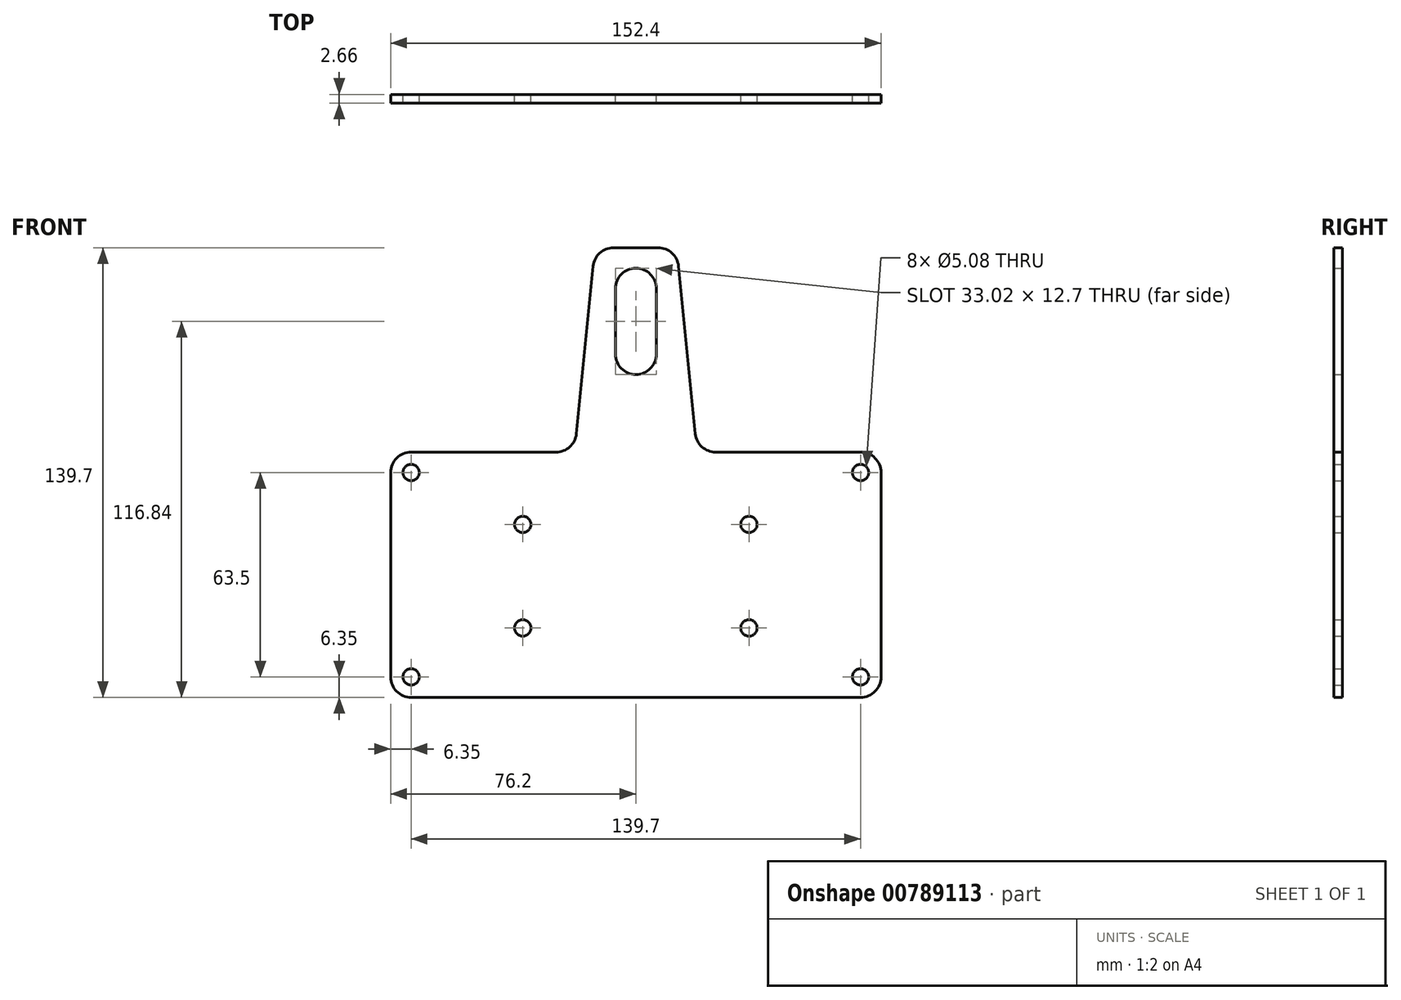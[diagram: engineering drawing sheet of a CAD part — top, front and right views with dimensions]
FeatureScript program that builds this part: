
annotation { "Feature Type Name" : "Feature", "Feature Type Description" : "" }
export const myFeature = defineFeature(function(context is Context, id is Id, definition is map)
    precondition{}
    {
        {
            var Q0;
            Q0=qCreatedBy(makeId("Front.planeOp"),FACE);
            var sketch = newSketch(context, id + "F0", { "sketchPlane" : qUnion([Q0])});
            skLineSegment(sketch, "E0", {"start": v(0, 0) * mm, "end": v(69.85, 0) * mm});
            skLineSegment(sketch, "E1", {"start": v(76.2, 6.35) * mm, "end": v(76.2, 69.85) * mm});
            skLineSegment(sketch, "E2", {"start": v(69.85, 76.2) * mm, "end": v(24.8, 76.2) * mm});
            skLineSegment(sketch, "E3", {"start": v(18.48, 81.92) * mm, "end": v(13.27, 133.98) * mm});
            skLineSegment(sketch, "E4", {"start": v(6.95, 139.7) * mm, "end": v(0, 139.7) * mm});
            skLineSegment(sketch, "E5", {"start": v(0, 139.7) * mm, "end": v(0, 0) * mm, "construction": true});
            skPoint(sketch, "E6.visualSharp", {"position": v(76.2, 0) * mm});
            skArc(sketch, "E6.filletArc", {"start": v(69.85, 0) * mm, "mid": v(74.34, 1.86) * mm, "end": v(76.2, 6.35) * mm});
            skPoint(sketch, "E7.visualSharp", {"position": v(76.2, 76.2) * mm});
            skArc(sketch, "E7.filletArc", {"start": v(76.2, 69.85) * mm, "mid": v(74.34, 74.34) * mm, "end": v(69.85, 76.2) * mm});
            skPoint(sketch, "E8.visualSharp", {"position": v(19.05, 76.2) * mm});
            skArc(sketch, "E8.filletArc", {"start": v(18.48, 81.92) * mm, "mid": v(20.54, 77.84) * mm, "end": v(24.8, 76.2) * mm});
            skPoint(sketch, "E9.visualSharp", {"position": v(12.7, 139.7) * mm});
            skArc(sketch, "E9.filletArc", {"start": v(13.27, 133.98) * mm, "mid": v(11.21, 138.06) * mm, "end": v(6.95, 139.7) * mm});
            skCircle(sketch, "E10", {"center": v(69.85, 69.85) * mm, "radius": 2.54 * mm});
            skCircle(sketch, "E11", {"center": v(69.85, 6.35) * mm, "radius": 2.54 * mm});
            skCircle(sketch, "E12", {"center": v(35.15, 21.57) * mm, "radius": 2.54 * mm});
            skCircle(sketch, "E13", {"center": v(35.15, 53.74) * mm, "radius": 2.54 * mm});
            skLineSegment(sketch, "E14.MirrorCS", {"start": v(-6.95, 139.7) * mm, "end": v(0, 139.7) * mm});
            skArc(sketch, "E15.MirrorCS", {"start": v(-13.27, 133.98) * mm, "mid": v(-11.21, 138.06) * mm, "end": v(-6.95, 139.7) * mm});
            skLineSegment(sketch, "E16.MirrorCS", {"start": v(-18.48, 81.92) * mm, "end": v(-13.27, 133.98) * mm});
            skArc(sketch, "E17.MirrorCS", {"start": v(-18.48, 81.92) * mm, "mid": v(-20.54, 77.84) * mm, "end": v(-24.8, 76.2) * mm});
            skLineSegment(sketch, "E18.MirrorCS", {"start": v(-69.85, 76.2) * mm, "end": v(-24.8, 76.2) * mm});
            skArc(sketch, "E19.MirrorCS", {"start": v(-76.2, 69.85) * mm, "mid": v(-74.34, 74.34) * mm, "end": v(-69.85, 76.2) * mm});
            skLineSegment(sketch, "E20.MirrorCS", {"start": v(-76.2, 6.35) * mm, "end": v(-76.2, 69.85) * mm});
            skPoint(sketch, "E21.MirrorP", {"position": v(-76.2, 0) * mm});
            skArc(sketch, "E22.MirrorCS", {"start": v(-69.85, 0) * mm, "mid": v(-74.34, 1.86) * mm, "end": v(-76.2, 6.35) * mm});
            skLineSegment(sketch, "E23.MirrorCS", {"start": v(0, 0) * mm, "end": v(-69.85, 0) * mm});
            skCircle(sketch, "E24.MirrorC", {"center": v(-69.85, 6.35) * mm, "radius": 2.54 * mm});
            skCircle(sketch, "E25.MirrorC", {"center": v(-35.15, 21.57) * mm, "radius": 2.54 * mm});
            skCircle(sketch, "E26.MirrorC", {"center": v(-35.15, 53.74) * mm, "radius": 2.54 * mm});
            skCircle(sketch, "E27.MirrorC", {"center": v(-69.85, 69.85) * mm, "radius": 2.54 * mm});
            skLineSegment(sketch, "E28", {"start": v(0, 127) * mm, "end": v(0, 106.68) * mm, "construction": true});
            skArc(sketch, "E29.0.startCap", {"start": v(-6.35, 127) * mm, "mid": v(0, 133.35) * mm, "end": v(6.35, 127) * mm});
            skArc(sketch, "E29.0.endCap", {"start": v(6.35, 106.68) * mm, "mid": v(0, 100.33) * mm, "end": v(-6.35, 106.68) * mm});
            skLineSegment(sketch, "E29.0.left", {"start": v(6.35, 127) * mm, "end": v(6.35, 106.68) * mm});
            skLineSegment(sketch, "E29.0.right", {"start": v(-6.35, 127) * mm, "end": v(-6.35, 106.68) * mm});
            skSolve(sketch);
        }
        {
            var Q0;
            Q0 = qSketchRegion(id + "F0", true);
            extrude(context, id + "F1", {"entities" : qUnion([Q0]), "depth" : 2.66 * mm, "offsetDistance" : 25.4 * mm});
        }
    });
